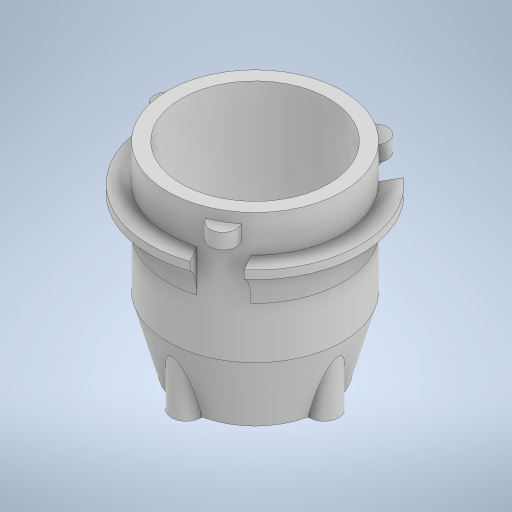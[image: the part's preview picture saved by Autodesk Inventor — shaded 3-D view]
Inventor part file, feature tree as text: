
AUTODESK INVENTOR PART (.ipt)
format: ipt  version: 2023.2 (Build 272271000, 271)  size: 411,136 bytes
history: native  units: mm
features: extrude x7, sketch x6, other x2, pattern_circular x2, revolve x1, fillet x1
ambient origin geometry x8: Origin, YZ Plane, XZ Plane, XY Plane, X Axis, Y Axis, Z Axis, Center Point
bodies: Body1 (feature_tree)
feature tree (19):
  other  "Поперечное сечение1"
  other  "Твердое тело1"
  sketch  "Эскиз1"
  extrude  "Выдавливание1"  Depth=26.1mm
  sketch  "Эскиз2"
  revolve  "Вращение1"
  extrude  "Выдавливание2"  Depth=30.9mm
  pattern_circular  "Круговой массив1"  [2 undecoded]
  extrude  "Выдавливание3"  Depth=12.25mm
  sketch  "Эскиз5"
  extrude  "Выдавливание4"  Depth=12.0mm
  extrude  "Выдавливание5"  Depth=10.85mm
  fillet  "Сопряжение1"  Radius=12.2mm
  sketch  "Эскиз6"
  extrude  "Выдавливание6"  TaperAngle=90.0deg  [1 undecoded]
  extrude  "Выдавливание7"  Depth=5.1mm
  pattern_circular  "Круговой массив2"  [2 undecoded]
  sketch  "Эскиз3"
  sketch  "Эскиз4"
note: 5 required parameter values undecoded (feature->parameter linkage not recoverable at this tier; creation-order binding heuristic only, values carry confidence <= 0.55)
